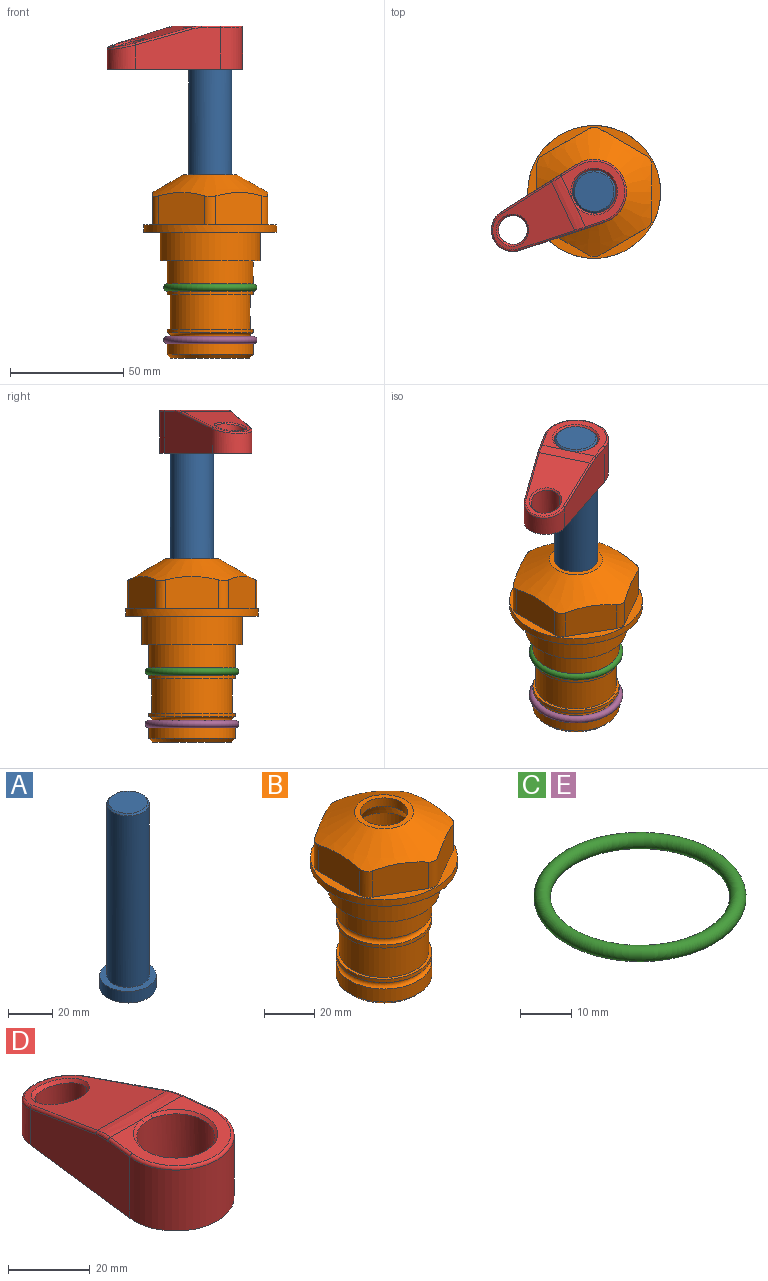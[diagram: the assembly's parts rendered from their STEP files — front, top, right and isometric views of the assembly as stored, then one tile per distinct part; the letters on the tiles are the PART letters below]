
ASSEMBLY  parts=5 mates=4
PART A: 6 faces, bbox 25.4x25.4x101.6 mm
  f0: plane 17.46x17.46mm, normal (0,0,1), area 239.5mm2, adj f5
  f1: plane 25.4x25.4mm, normal (0,0,-1), area 506.7mm2, adj f2
  f2: cylinder r=12.7mm len=25.4mm, axis (0,0,1), area 506.7mm2, adj f1,f3
  f3: plane 25.4x25.4mm, normal (0,0,1), area 221.7mm2, adj f2,f4
  f4: cylinder r=9.53mm len=94.46mm, axis (0,0,1), area 5653mm2, adj f3,f5
  f5: cone r=8.73mm half-angle=45deg, axis (0,0,-1), area 64.4mm2, adj f0,f4
PART B: 36 faces, bbox 58.7x58.7x81 mm
  f0: cylinder r=17.78mm len=35.56mm, axis (0,0,1), area 1670.8mm2, adj f23,f24,f31
  f1: cylinder r=19.05mm len=38.1mm, axis (0,0,1), area 1191.9mm2, adj f26,f27,f30
  f2: plane 58.66x58.66mm, normal (0,0,-1), area 1150.6mm2, adj f3,f28
  f3: cylinder r=29.33mm len=58.66mm, axis (0,0,-1), area 585.1mm2, adj f2,f4
  f4: plane 58.66x58.66mm, normal (0,0,1), area 475.9mm2, adj f3,f5,f6,f7,f8,f9,f10,f11
  f5: plane 20.32x14.34mm, normal (-0.5,0.87,0), area 324.4mm2, adj f4,f15,f16,f17
  f6: plane 20.32x14.34mm, normal (0.5,0.87,0), area 324.4mm2, adj f4,f14,f15,f17
  f7: plane 23.48x14.34mm, normal (1,0,0), area 324.4mm2, adj f4,f13,f14,f17
  f8: plane 20.32x14.34mm, normal (0.5,-0.87,0), area 324.4mm2, adj f4,f12,f13,f17
  f9: plane 20.32x14.34mm, normal (-0.5,-0.87,0), area 324.4mm2, adj f4,f11,f12,f17
  f10: plane 23.48x14.34mm, normal (-1,0,0), area 324.4mm2, adj f4,f11,f16,f17
  f11: cylinder r=5.08mm len=12.85mm, axis (0,0,-1), area 67.2mm2, adj f4,f9,f10,f17
  f12: cylinder r=5.08mm len=12.85mm, axis (0,0,-1), area 67.2mm2, adj f4,f8,f9,f17
  f13: cylinder r=5.08mm len=12.85mm, axis (0,0,-1), area 67.2mm2, adj f4,f7,f8,f17
  f14: cylinder r=5.08mm len=12.85mm, axis (0,0,-1), area 67.2mm2, adj f4,f6,f7,f17
  f15: cylinder r=5.08mm len=12.85mm, axis (0,0,-1), area 67.2mm2, adj f4,f5,f6,f17
  f16: cylinder r=5.08mm len=12.85mm, axis (0,0,-1), area 67.2mm2, adj f4,f5,f10,f17
  f17: cone r=11.73mm half-angle=60deg, axis (0,0,-1), area 2071.8mm2, adj f5,f6,f7,f8,f9,f10,f11,f12
  f18: plane 23.46x23.46mm, normal (0,0,1), area 147.4mm2, adj f17,f35
  f19: plane 34.93x34.93mm, normal (0,0,-1), area 958mm2, adj f29
  f20: cylinder r=19.05mm len=38.1mm, axis (0,0,1), area 760.1mm2, adj f21,f29
  f21: torus R=19.05mm, axis (0,0,1), area 565.3mm2, adj f20,f22
  f22: cylinder r=19.05mm len=38.1mm, axis (0,0,1), area 190mm2, adj f21,f23
  f23: plane 38.1x38.1mm, normal (0,0,1), area 146.9mm2, adj f0,f22
  f24: plane 38.1x38.1mm, normal (0,0,-1), area 146.9mm2, adj f0,f25
  f25: cylinder r=19.05mm len=38.1mm, axis (0,0,1), area 190mm2, adj f24,f26
  f26: torus R=19.05mm, axis (0,0,1), area 565.3mm2, adj f1,f25
  f27: plane 44.45x44.45mm, normal (0,0,-1), area 411.7mm2, adj f1,f28
  f28: cylinder r=22.23mm len=44.45mm, axis (0,0,1), area 1773.5mm2, adj f2,f27
  f29: cone r=19.05mm half-angle=45deg, axis (0,0,1), area 257.5mm2, adj f19,f20
  f30: cylinder r=3.17mm len=6.75mm, axis (-1,0,0), area 128mm2, adj f1,f33
  f31: cylinder r=3.17mm len=6.35mm, axis (-1,0,0), area 102.5mm2, adj f0,f33
  f32: plane 25.4x25.4mm, normal (0,0,1), area 506.7mm2, adj f33
  f33: cylinder r=12.7mm len=66.42mm, axis (0,0,-1), area 5236.2mm2, adj f30,f31,f32,f34
  f34: cone r=9.53mm half-angle=30deg, axis (0,0,-1), area 443.4mm2, adj f33,f35
  f35: cylinder r=9.53mm len=19.05mm, axis (0,0,-1), area 240.9mm2, adj f18,f34
PART C: 1 faces, bbox 44.7x44.7x3.2 mm
  f0: torus R=19.05mm, axis (0,0,1), area 1193.9mm2
PART D: 31 faces, bbox 31.7x65.5x19.8 mm
  f0: plane 39.12x18.26mm, normal (0.99,0.12,0), area 612.2mm2, adj f1,f4,f7,f11,f13,f15
  f1: cylinder r=9.53mm len=18.91mm, axis (0,0,-1), area 296.1mm2, adj f0,f2,f7,f17
  f2: plane 39.12x18.26mm, normal (-0.99,0.12,0), area 612.2mm2, adj f1,f4,f7,f12,f14,f16
  f3: cylinder r=6.35mm len=12.7mm, axis (0,0,-1), area 362.4mm2, adj f7,f18
  f4: cylinder r=14.29mm len=28.58mm, axis (0,0,-1), area 882.2mm2, adj f0,f2,f7,f10
  f5: cylinder r=9.53mm len=19.05mm, axis (0,0,-1), area 1092.6mm2, adj f7,f19,f20
  f6: plane 26.99x23.69mm, normal (0,0,1), area 216.2mm2, adj f9,f10,f11,f12,f19
  f7: plane 63.5x28.58mm, normal (0,0,-1), area 661.8mm2, adj f0,f1,f2,f3,f4,f5,f22,f23
  f8: plane 33.52x23.6mm, normal (0,0.26,0.97), area 486mm2, adj f9,f15,f16,f17,f18
  f9: cylinder r=19.05mm len=24.72mm, axis (1,0,0), area 120.4mm2, adj f6,f8,f13,f14,f20
  f10: torus R=13.49mm, axis (0,0,1), area 59mm2, adj f4,f6,f11,f12
  f11: cylinder r=0.79mm len=8.67mm, axis (0.12,-0.99,0), area 10.8mm2, adj f0,f6,f10,f13
  f12: cylinder r=0.79mm len=8.67mm, axis (0.12,0.99,0), area 10.8mm2, adj f2,f6,f10,f14
  f13: bspline ~4.95x1.42mm, area 6.1mm2, adj f0,f9,f11,f15
  f14: bspline ~4.95x1.42mm, area 6.1mm2, adj f2,f9,f12,f16
  f15: cylinder r=0.79mm len=25.95mm, axis (0.12,-0.96,0.26), area 32.9mm2, adj f0,f8,f13,f17
  f16: cylinder r=0.79mm len=25.95mm, axis (0.12,0.96,-0.26), area 32.9mm2, adj f2,f8,f14,f17
  f17: bspline ~18.91x8.38mm, area 30mm2, adj f1,f8,f15,f16
  f18: bspline ~14.29x14.29mm, area 48.3mm2, adj f3,f8
  f19: cone r=9.53mm half-angle=45deg, axis (0,0,1), area 66.5mm2, adj f5,f6,f20
  f20: bspline ~3.22x0.96mm, area 3.5mm2, adj f5,f9,f19
  f21: plane 2.75x2.72mm, normal (0,0,-1), area 2.9mm2, adj f23,f25,f28
  f22: plane 23.05x15.88mm, normal (-0.99,-0.12,0), area 323.6mm2, adj f7,f25,f26,f27,f28,f29
  f23: plane 23.05x15.88mm, normal (0.99,-0.12,0), area 323.6mm2, adj f7,f21,f25,f27,f28,f30
  f24: cylinder r=9.53mm len=10.69mm, axis (0,0,-1), area 114.7mm2, adj f7,f27,f29,f30
  f25: cylinder r=12.7mm len=20.59mm, axis (0,0,-1), area 381.1mm2, adj f7,f21,f22,f23,f26,f28
  f26: plane 2.75x2.72mm, normal (0,0,-1), area 2.9mm2, adj f22,f25,f28
  f27: plane 19.72x18.37mm, normal (0,-0.26,-0.97), area 291.8mm2, adj f22,f23,f24,f28,f29,f30
  f28: cylinder r=15.88mm len=19.92mm, axis (1,0,0), area 54.8mm2, adj f21,f22,f23,f25,f26,f27
  f29: cylinder r=1.59mm len=11mm, axis (0,0,-1), area 34.7mm2, adj f7,f22,f24,f27
  f30: cylinder r=1.59mm len=11mm, axis (0,0,-1), area 34.7mm2, adj f7,f23,f24,f27
PART E: same geometry as C
PLACE A rot(axis=(0,0,1),115.2deg) t=(0,0,27.55)mm
PLACE B at identity fixed
PLACE C at identity
PLACE D rot(axis=(0,0,1),115.2deg) t=(0,0,27.55)mm
PLACE E t=(0,0,-23.18)mm
MATE fastened B.f0 <-> E.f0  axis (0,0,1) through (0,0,-47.69)mm
MATE fastened C.f0 <-> B.f0  axis (0,0,1) through (0,0,-24.51)mm
MATE cylindrical B.f0 <-> A.f2  axis (0,0,1) through (0,0,-50.55)mm
MATE fastened A.f2 <-> D.f4  axis (0,0,1) through (0,0,91.05)mm
